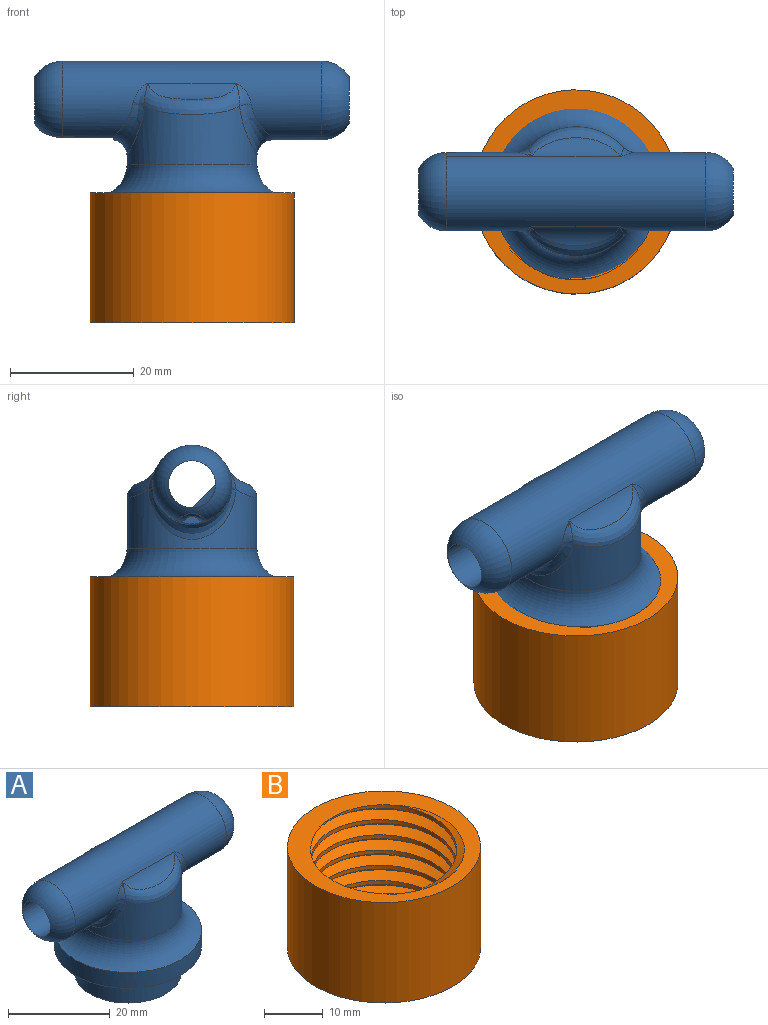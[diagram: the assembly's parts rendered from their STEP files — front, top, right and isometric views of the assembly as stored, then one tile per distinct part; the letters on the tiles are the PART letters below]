
ASSEMBLY  parts=2 mates=1
PART A: 41 faces, bbox 51.5x34.4x32.5 mm
  f0: cylinder r=10.5mm len=21mm, axis (0,0,-1), area 418.9mm2, adj f10,f39
  f1: plane 1.63x0mm, normal (0,0,1), area 0mm2, adj f5,f7,f11,f15
  f2: plane 1.63x0mm, normal (0,0,1), area 0mm2, adj f6,f7,f11,f14
  f3: plane 1.63x0mm, normal (0,0,1), area 0mm2, adj f6,f7,f11,f14
  f4: plane 1.63x0mm, normal (0,0,1), area 0mm2, adj f5,f8,f11,f15
  f5: cylinder r=3.81mm len=7.62mm, axis (1,0,0), area 16.9mm2, adj f1,f4,f7,f8,f15
  f6: cylinder r=3.81mm len=7.62mm, axis (1,0,0), area 14.2mm2, adj f2,f3,f7,f14
  f7: cylinder r=9mm len=25.4mm, axis (0,0,-1), area 1283.5mm2, adj f1,f2,f3,f5,f6,f8,f10,f11
  f8: cylinder r=9mm len=2.54mm, axis (0,0,-1), area 0mm2, adj f4,f5,f7,f11
  f9: cylinder r=10.5mm len=21mm, axis (0,0,-1), area 409.5mm2, adj f23,f26,f27,f30,f40
  f10: plane 21x21mm, normal (0,0,-1), area 91.9mm2, adj f0,f7
  f11: cylinder r=3.81mm len=50.8mm, axis (-1,0,0), area 393.3mm2, adj f1,f2,f3,f4,f7,f8,f14,f15
  f12: cylinder r=6.35mm len=42mm, axis (-1,0,0), area 971.8mm2, adj f13,f16,f17,f18,f19,f25,f26,f27
  f13: cylinder r=6.35mm len=13.81mm, axis (-1,0,0), area 112.3mm2, adj f12,f18,f24,f26,f34,f37
  f14: cylinder r=10.5mm len=7.62mm, axis (0,0,-1), area 0.1mm2, adj f2,f3,f6,f11
  f15: cylinder r=10.5mm len=7.62mm, axis (0,0,-1), area 0.1mm2, adj f1,f4,f5,f11
  f16: cylinder r=5.08mm len=14.37mm, axis (-1,0,0), area 36mm2, adj f12,f23
  f17: cylinder r=5.08mm len=14.37mm, axis (-1,0,0), area 36mm2, adj f12,f30
  f18: torus R=1.27mm, axis (-1,0,0), area 167mm2, adj f11,f12,f13,f20,f36
  f19: torus R=1.27mm, axis (1,0,0), area 182.9mm2, adj f11,f12,f20
  f20: cylinder r=3.81mm len=50.8mm, axis (1,0,0), area 608.6mm2, adj f11,f18,f19
  f21: plane 10.43x2.65mm, normal (0,0,-1), area 19.4mm2, adj f11,f31
  f22: plane 10.43x2.65mm, normal (0,0,-1), area 19.4mm2, adj f11,f32
  f23: bspline ~19.37x6.45mm, area 55.5mm2, adj f9,f16,f24,f25
  f24: bspline ~4.33x2.43mm, area 3.1mm2, adj f13,f23,f26
  f25: bspline ~4.33x2.43mm, area 3mm2, adj f12,f23,f27
  f26: bspline ~14.32x9.36mm, area 65.7mm2, adj f9,f12,f13,f24,f28,f34
  f27: bspline ~14.32x9.36mm, area 65.7mm2, adj f9,f12,f25,f29
  f28: bspline ~4.33x2.43mm, area 3mm2, adj f12,f26,f30
  f29: bspline ~4.33x2.43mm, area 3.1mm2, adj f12,f27,f30
  f30: bspline ~19.32x6.46mm, area 55.5mm2, adj f9,f17,f28,f29
  f31: torus R=6.46mm, axis (0,0,1), area 71.3mm2, adj f7,f11,f21
  f32: torus R=6.46mm, axis (0,0,1), area 71.3mm2, adj f7,f11,f22
  f33: cylinder r=1.27mm len=11.09mm, axis (1,0,0), area 22.4mm2, adj f34,f35,f36,f37
  f34: plane 5.42x1.92mm, normal (-1,0,0), area 2.7mm2, adj f12,f13,f26,f33,f35,f37
  f35: cylinder r=1.27mm len=8.3mm, axis (-1,0,0), area 12.9mm2, adj f12,f33,f34,f36
  f36: bspline ~4.86x4.74mm, area 11mm2, adj f18,f33,f35,f37
  f37: cylinder r=1.27mm len=8.3mm, axis (1,0,0), area 12.9mm2, adj f13,f33,f34,f36
  f38: cylinder r=14.48mm len=28.95mm, axis (0,0,-1), area 346.5mm2, adj f39,f40
  f39: plane 28.95x28.95mm, normal (0,0,-1), area 311.9mm2, adj f0,f38
  f40: torus R=15.58mm, axis (0,0,-1), area 513.9mm2, adj f9,f38
PART B: 7 faces, bbox 34x34x24.4 mm
  f0: cylinder r=16.5mm len=33mm, axis (0,0,-1), area 2177.1mm2, adj f1,f2
  f1: plane 33.88x33.88mm, normal (0,0,1), area 308.9mm2, adj f0,f3,f4,f5,f6
  f2: plane 33.97x33.97mm, normal (0,0,-1), area 308.9mm2, adj f0,f3,f4,f5,f6
  f3: bspline ~32.63x28.26mm, area 1092.7mm2, adj f1,f2,f5,f6
  f4: bspline ~32.63x28.26mm, area 1093.1mm2, adj f1,f2,f5,f6
  f5: bspline ~32.97x28.55mm, area 268.6mm2, adj f1,f2,f3,f4
  f6: cylinder r=12.41mm len=24.82mm, axis (0,0,1), area 504.6mm2, adj f1,f2,f3,f4
PLACE A at identity
PLACE B rot(axis=(1,0,0),0deg) t=(0,0,-10.5)mm
MATE revolute B.f0 <-> A.f7  axis (0,0,-1) through (0,0,0)mm
